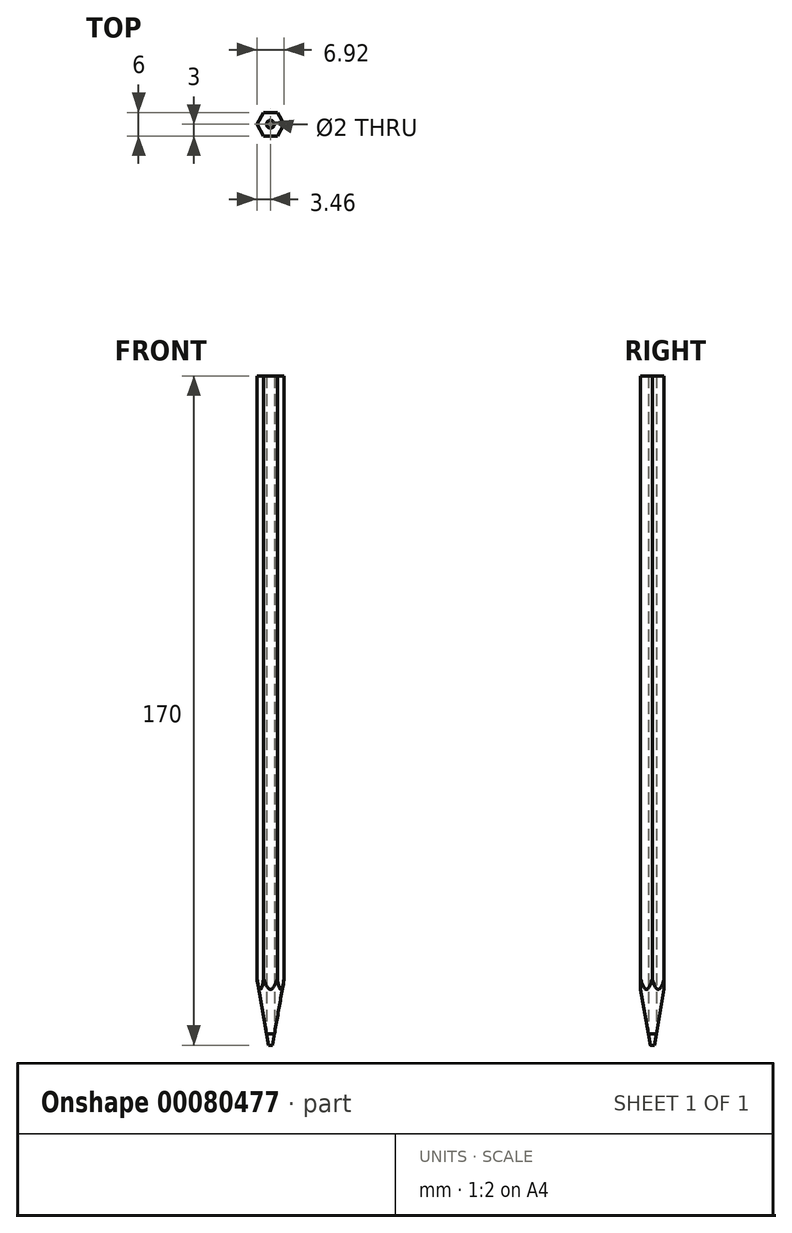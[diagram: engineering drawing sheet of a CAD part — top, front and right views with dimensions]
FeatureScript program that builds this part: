
annotation { "Feature Type Name" : "Feature", "Feature Type Description" : "" }
export const myFeature = defineFeature(function(context is Context, id is Id, definition is map)
    precondition{}
    {
        {
            var Q0;
            Q0=qCreatedBy(makeId("Top.planeOp"),FACE);
            var sketch = newSketch(context, id + "F0", { "sketchPlane" : qUnion([Q0])});
            skCircle(sketch, "E0.cCircle", {"center": v(0, 0) * mm, "radius": 3 * mm, "construction": true});
            skLineSegment(sketch, "E0.0", {"start": v(-1.73, 3) * mm, "end": v(1.73, 3) * mm});
            skLineSegment(sketch, "E0.1", {"start": v(1.73, 3) * mm, "end": v(3.46, 0) * mm});
            skLineSegment(sketch, "E0.2", {"start": v(3.46, 0) * mm, "end": v(1.73, -3) * mm});
            skLineSegment(sketch, "E0.3", {"start": v(1.73, -3) * mm, "end": v(-1.73, -3) * mm});
            skLineSegment(sketch, "E0.4", {"start": v(-1.73, -3) * mm, "end": v(-3.46, 0) * mm});
            skLineSegment(sketch, "E0.5", {"start": v(-3.46, 0) * mm, "end": v(-1.73, 3) * mm});
            skPoint(sketch, "E0.0.midPoint", {"position": v(0, 3) * mm});
            skCircle(sketch, "E1", {"center": v(0, 0) * mm, "radius": 1 * mm});
            skSolve(sketch);
        }
        {
            var Q0;
            Q0 = qSketchRegion(id + "F0", true);
            extrude(context, id + "F1", {"entities" : qUnion([Q0]), "depth" : 170 * mm});
        }
        {
            var Q0;
            Q0=makeQuery(id+"F0.imprint","IMPRINT",FACE,{"disambiguationData":[TD([[makeQuery(id+"F0.imprint","IMPRINT",EDGE,{"derivedFrom":sQuery(id+"F0.wireOp",EDGE,"E1")}),1.0]])]});
            extrude(context, id + "F2", {"entities" : qUnion([Q0]), "depth" : 170 * mm});
        }
        {
            var Q0;
            Q0=qCreatedBy(makeId("Front.planeOp"),FACE);
            var sketch = newSketch(context, id + "F3", { "sketchPlane" : qUnion([Q0])});
            skLineSegment(sketch, "E2", {"start": v(0.5, 0) * mm, "end": v(4.08, 20.32) * mm});
            skLineSegment(sketch, "E3", {"start": v(4.08, 20.32) * mm, "end": v(4.08, 0) * mm});
            skLineSegment(sketch, "E4", {"start": v(4.08, 0) * mm, "end": v(0.5, 0) * mm});
            skLineSegment(sketch, "E5", {"start": v(0, 0) * mm, "end": v(0, -4.03) * mm, "construction": true});
            skSolve(sketch);
        }
        {
            var Q0;
            Q0=makeQuery(id+"F3.imprint","IMPRINT",FACE,{"disambiguationData":[TD([[makeQuery(id+"F3.imprint","IMPRINT",EDGE,{"derivedFrom":sQuery(id+"F3.wireOp",EDGE,"E2")}),-1.0]])]});
            var Q1;
            Q1=sQuery(id+"F3.wireOp",EDGE,"E5");
            revolve(context, id + "F4", {"operationType" : NewBodyOperationType.REMOVE, "entities" : qUnion([Q0]), "axis" : qUnion([Q1]), "revolveType" : RevolveType.FULL, "oppositeDirection" : true});
        }
    });
